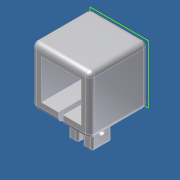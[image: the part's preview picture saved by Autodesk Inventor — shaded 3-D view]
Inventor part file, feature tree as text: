
AUTODESK INVENTOR PART (.ipt)
format: ipt  version: unknown  size: 297,984 bytes
history: native  units: in
note: dims shown in document units (in); Inventor stores cm internally (conversion verified against a paired STEP export)
features: fillet x10, extrude x5, sketch x5
ambient origin geometry x8: Origin, YZ Plane, XZ Plane, XY Plane, X Axis, Y Axis, Z Axis, Center Point
bodies: Solid1 (feature_tree)
feature tree (20):
  extrude  "Extrusion1"  Depth=0.5in TaperAngle=0.0deg
  extrude  "Extrusion6"  Depth=0.7in TaperAngle=0.0deg
  sketch  "Sketch8"  dims[d50=3.0in d51=0.0in d52=0.125in]
  sketch  "Sketch9"  dims[d53=0.125in d54=0.125in]
  extrude  "Extrusion7"  Depth=0.125in
  extrude  "Extrusion8"  Depth=0.125in
  extrude  "Extrusion9"  Depth=0.125in
  fillet  "Fillet9"  Radius=0.125in
  fillet  "Fillet10"  Radius=0.05in
  fillet  "Fillet11"  Radius=0.05in
  fillet  "Fillet12"  Radius=0.05in
  fillet  "Fillet13"  Radius=0.05in
  fillet  "Fillet14"  [1 undecoded]
  fillet  "Fillet15"  [1 undecoded]
  fillet  "Fillet16"  [1 undecoded]
  fillet  "Fillet17"  [1 undecoded]
  fillet  "Fillet18"  [1 undecoded]
  sketch  "Sketch1"  dims[d6=1.5in d7=0.0in d37=0.5in d38=0.0in]
  sketch  "Sketch7"  dims[d45=0.7in d46=0.0in d47=0.7in d48=0.0in]
  sketch  "Sketch10"  dims[d55=0.125in d56=0.125in d57=0.125in d58=0.05in d59=0.05in d60=0.05in d61=0.05in]
note: 5 required parameter values undecoded (feature->parameter linkage not recoverable at this tier; creation-order binding heuristic only, values carry confidence <= 0.55)
